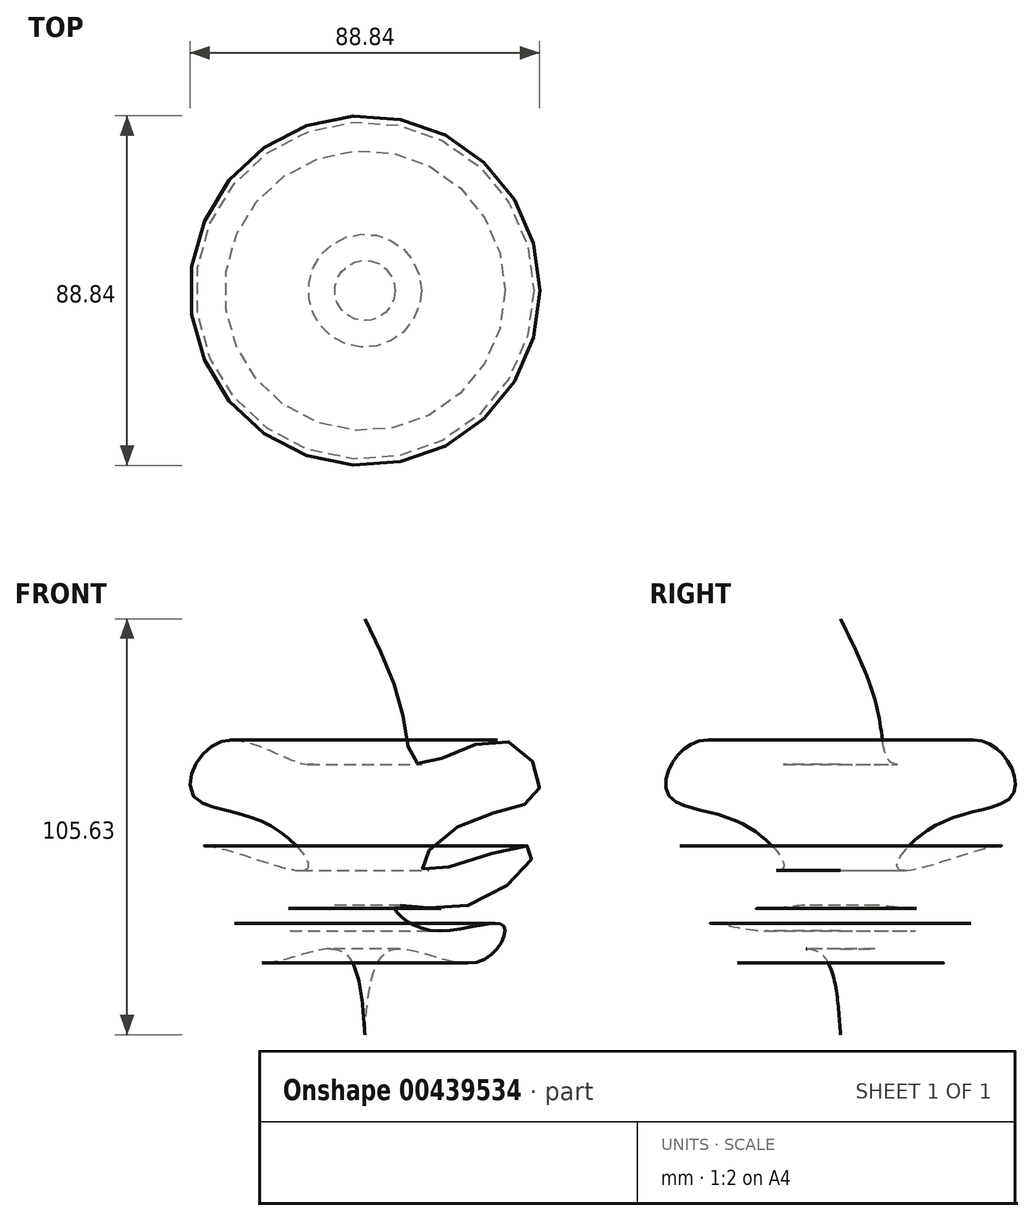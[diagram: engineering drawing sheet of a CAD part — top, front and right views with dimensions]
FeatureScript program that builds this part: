
annotation { "Feature Type Name" : "Feature", "Feature Type Description" : "" }
export const myFeature = defineFeature(function(context is Context, id is Id, definition is map)
    precondition{}
    {
        {
            var Q0;
            Q0=qCreatedBy(makeId("Front.planeOp"),FACE);
            var sketch = newSketch(context, id + "F0", { "sketchPlane" : qUnion([Q0])});
            skFitSpline(sketch, "E0", {"points": [v(0, -35.76) * mm, v(6.82, -14.2) * mm, v(29.13, -17.15) * mm, v(35.21, -8.11) * mm, v(16.6, -9.22) * mm, v(7.74, -3.32) * mm, v(27.47, -2.58) * mm, v(42.22, 11.98) * mm, v(15.12, 6.08) * mm, v(24.7, 17.7) * mm, v(44.06, 25.8) * mm, v(35.58, 38.9) * mm, v(13.83, 33) * mm, v(9.77, 44.98) * mm, v(0, 69.87) * mm], "startDerivative": vector(26, 380.86) * mm, "endDerivative": vector(-144.72, 291.73) * mm});
            skLineSegment(sketch, "E1", {"start": v(0, 69.87) * mm, "end": v(0, -35.76) * mm});
            skSolve(sketch);
        }
        {
            var Q0;
            Q0=makeQuery(id+"F0.imprint","IMPRINT",FACE,{"disambiguationData":[TD([[makeQuery(id+"F0.imprint","IMPRINT",EDGE,{"derivedFrom":sQuery(id+"F0.wireOp",EDGE,"E0")}),1.0]])]});
            var Q1;
            Q1=sQuery(id+"F0.wireOp",EDGE,"E1");
            revolve(context, id + "F1", {"entities" : qUnion([Q0]), "axis" : qUnion([Q1]), "revolveType" : RevolveType.FULL});
        }
    });
